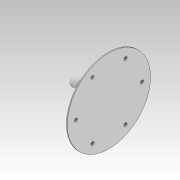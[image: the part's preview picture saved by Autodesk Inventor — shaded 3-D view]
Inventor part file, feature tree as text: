
AUTODESK INVENTOR PART (.ipt)
format: ipt  version: 2020 (Build 240168000, 168)  size: 148,992 bytes
history: native  units: mm
features: sketch x3, extrude x2, revolve x1, plane x1, pattern_circular x1
ambient origin geometry x8: Origin, YZ Plane, XZ Plane, XY Plane, X Axis, Y Axis, Z Axis, Center Point
bodies: Solid1 (feature_tree)
feature tree (8):
  revolve  "Revolution1"  [1 undecoded]
  extrude  "Extrusion1"  Depth=3.0mm
  plane  "Work Plane1"
  extrude  "Extrusion2"  Depth=10.0mm
  pattern_circular  "Circular Pattern1"  Angle=90.0deg  [1 undecoded]
  sketch  "Sketch1"  dims[d0=44.0mm d1=5.0mm]
  sketch  "Sketch2"  dims[d2=3.0mm d3=1.0mm]
  sketch  "Sketch3"  dims[d4=35.0mm d5=10.0mm d6=90.0deg d7=3.3mm d8=35.0mm d9=0.0mm d10=0.0mm d11=-2.0mm d12=6.0mm d13=2.0mm d14=0.0mm d15=60.0mm d16=360.0deg]
note: 2 required parameter values undecoded (feature->parameter linkage not recoverable at this tier; creation-order binding heuristic only, values carry confidence <= 0.55)